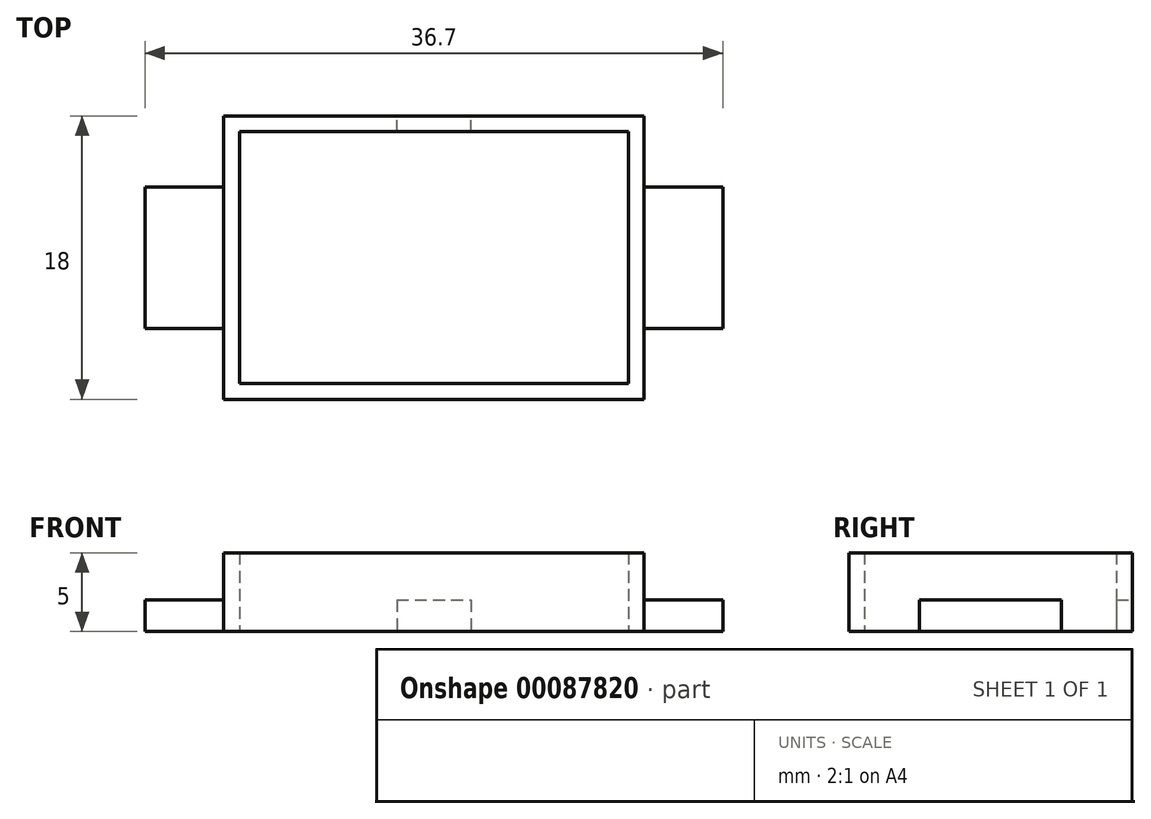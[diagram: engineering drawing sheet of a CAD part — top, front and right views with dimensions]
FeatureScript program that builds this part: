
annotation { "Feature Type Name" : "Feature", "Feature Type Description" : "" }
export const myFeature = defineFeature(function(context is Context, id is Id, definition is map)
    precondition{}
    {
        {
            var Q0;
            Q0=qCreatedBy(makeId("Top.planeOp"),FACE);
            var sketch = newSketch(context, id + "F0", { "sketchPlane" : qUnion([Q0])});
            skLineSegment(sketch, "E0.bottom", {"start": v(0, 0) * mm, "end": v(22.7, 0) * mm});
            skLineSegment(sketch, "E0.top", {"start": v(0, 14) * mm, "end": v(22.7, 14) * mm});
            skLineSegment(sketch, "E0.left", {"start": v(0, 0) * mm, "end": v(0, 4.5) * mm});
            skLineSegment(sketch, "E0.right", {"start": v(22.7, 0) * mm, "end": v(22.7, 4.5) * mm});
            skLineSegment(sketch, "E1.bottom", {"start": v(0, 4.5) * mm, "end": v(-5, 4.5) * mm});
            skLineSegment(sketch, "E1.top", {"start": v(0, 9.5) * mm, "end": v(-5, 9.5) * mm});
            skLineSegment(sketch, "E1.left", {"start": v(0, 4.5) * mm, "end": v(0, 9.5) * mm});
            skLineSegment(sketch, "E1.right", {"start": v(-5, 4.5) * mm, "end": v(-5, 9.5) * mm});
            skLineSegment(sketch, "E2.bottom", {"start": v(22.7, 4.5) * mm, "end": v(27.7, 4.5) * mm});
            skLineSegment(sketch, "E2.top", {"start": v(22.7, 9.5) * mm, "end": v(27.7, 9.5) * mm});
            skLineSegment(sketch, "E2.left", {"start": v(22.7, 4.5) * mm, "end": v(22.7, 9.5) * mm});
            skLineSegment(sketch, "E2.right", {"start": v(27.7, 4.5) * mm, "end": v(27.7, 9.5) * mm});
            skLineSegment(sketch, "E3", {"start": v(22.7, 9.5) * mm, "end": v(22.7, 14) * mm});
            skLineSegment(sketch, "E4", {"start": v(0, 9.5) * mm, "end": v(0, 14) * mm});
            skLineSegment(sketch, "E5.0", {"start": v(-2, 11.5) * mm, "end": v(-2, 16) * mm});
            skLineSegment(sketch, "E5.1", {"start": v(24.7, 2.5) * mm, "end": v(29.7, 2.5) * mm});
            skLineSegment(sketch, "E5.2", {"start": v(29.7, 2.5) * mm, "end": v(29.7, 11.5) * mm});
            skLineSegment(sketch, "E5.3", {"start": v(24.7, 11.5) * mm, "end": v(29.7, 11.5) * mm});
            skLineSegment(sketch, "E5.4", {"start": v(24.7, 11.5) * mm, "end": v(24.7, 16) * mm});
            skLineSegment(sketch, "E5.5", {"start": v(24.7, -2) * mm, "end": v(24.7, 2.5) * mm});
            skLineSegment(sketch, "E5.6", {"start": v(-2, 16) * mm, "end": v(24.7, 16) * mm});
            skLineSegment(sketch, "E5.7", {"start": v(-2, -2) * mm, "end": v(24.7, -2) * mm});
            skLineSegment(sketch, "E5.8", {"start": v(-2, -2) * mm, "end": v(-2, 2.5) * mm});
            skLineSegment(sketch, "E5.9", {"start": v(-2, 2.5) * mm, "end": v(-7, 2.5) * mm});
            skLineSegment(sketch, "E5.10", {"start": v(-7, 2.5) * mm, "end": v(-7, 11.5) * mm});
            skLineSegment(sketch, "E5.11", {"start": v(-2, 11.5) * mm, "end": v(-7, 11.5) * mm});
            skLineSegment(sketch, "E6.0", {"start": v(-1, 10.5) * mm, "end": v(-1, 15) * mm});
            skLineSegment(sketch, "E6.1", {"start": v(23.7, 3.5) * mm, "end": v(28.7, 3.5) * mm});
            skLineSegment(sketch, "E6.2", {"start": v(28.7, 3.5) * mm, "end": v(28.7, 10.5) * mm});
            skLineSegment(sketch, "E6.3", {"start": v(23.7, 10.5) * mm, "end": v(28.7, 10.5) * mm});
            skLineSegment(sketch, "E6.4", {"start": v(23.7, 10.5) * mm, "end": v(23.7, 15) * mm});
            skLineSegment(sketch, "E6.5", {"start": v(23.7, -1) * mm, "end": v(23.7, 3.5) * mm});
            skLineSegment(sketch, "E6.6", {"start": v(-1, 15) * mm, "end": v(23.7, 15) * mm});
            skLineSegment(sketch, "E6.7", {"start": v(-1, -1) * mm, "end": v(23.7, -1) * mm});
            skLineSegment(sketch, "E6.8", {"start": v(-1, -1) * mm, "end": v(-1, 3.5) * mm});
            skLineSegment(sketch, "E6.9", {"start": v(-1, 3.5) * mm, "end": v(-6, 3.5) * mm});
            skLineSegment(sketch, "E6.10", {"start": v(-6, 3.5) * mm, "end": v(-6, 10.5) * mm});
            skLineSegment(sketch, "E6.11", {"start": v(-1, 10.5) * mm, "end": v(-6, 10.5) * mm});
            skLineSegment(sketch, "E7", {"start": v(9, 14) * mm, "end": v(9, 16) * mm});
            skLineSegment(sketch, "E8", {"start": v(13.7, 14) * mm, "end": v(13.7, 16) * mm});
            skLineSegment(sketch, "E9", {"start": v(-1, 10.5) * mm, "end": v(-1, 3.5) * mm});
            skLineSegment(sketch, "E10", {"start": v(23.7, 10.5) * mm, "end": v(23.7, 3.5) * mm});
            skLineSegment(sketch, "E11", {"start": v(-2, 11.5) * mm, "end": v(-2, 2.5) * mm});
            skLineSegment(sketch, "E12", {"start": v(24.7, 11.5) * mm, "end": v(24.7, 2.5) * mm});
            skSolve(sketch);
        }
        {
            var Q0;
            {var subQ0=sQuery(id+"F0.wireOp",EDGE,"E2.right");Q0=makeQuery(id+"F0.imprint","IMPRINT",FACE,{"disambiguationData":[TD([[makeQuery(id+"F0.imprint","IMPRINT",EDGE,{"derivedFrom":subQ0}),1.0]])]});}
            var Q1;
            {var subQ10=sQuery(id+"F0.wireOp",EDGE,"E5.0");Q1=makeQuery(id+"F0.imprint","IMPRINT",FACE,{"disambiguationData":[TD([[makeQuery(id+"F0.imprint","IMPRINT",EDGE,{"derivedFrom":subQ10}),-1.0]])]});}
            var Q2;
            {var subQ0=sQuery(id+"F0.wireOp",EDGE,"E1.right");Q2=makeQuery(id+"F0.imprint","IMPRINT",FACE,{"disambiguationData":[TD([[makeQuery(id+"F0.imprint","IMPRINT",EDGE,{"derivedFrom":subQ0}),-1.0]])]});}
            var Q3;
            {var subQ1=sQuery(id+"F0.wireOp",EDGE,"E1.right");Q3=makeQuery(id+"F0.imprint","IMPRINT",FACE,{"disambiguationData":[TD([[makeQuery(id+"F0.imprint","IMPRINT",EDGE,{"derivedFrom":subQ1}),1.0]])]});}
            var Q4;
            {var subQ1=sQuery(id+"F0.wireOp",EDGE,"E2.right");Q4=makeQuery(id+"F0.imprint","IMPRINT",FACE,{"disambiguationData":[TD([[makeQuery(id+"F0.imprint","IMPRINT",EDGE,{"derivedFrom":subQ1}),-1.0]])]});}
            var Q5;
            {var subQ5=sQuery(id+"F0.wireOp",EDGE,"E5.9");Q5=makeQuery(id+"F0.imprint","IMPRINT",FACE,{"disambiguationData":[TD([[makeQuery(id+"F0.imprint","IMPRINT",EDGE,{"derivedFrom":subQ5}),-1.0]])]});}
            var Q6;
            {var subQ8=sQuery(id+"F0.wireOp",EDGE,"E5.5");Q6=makeQuery(id+"F0.imprint","IMPRINT",FACE,{"disambiguationData":[TD([[makeQuery(id+"F0.imprint","IMPRINT",EDGE,{"derivedFrom":subQ8}),1.0]])]});}
            var Q7;
            {var subQ0=sQuery(id+"F0.wireOp",EDGE,"E9");var subQ1=sQuery(id+"F0.wireOp",EDGE,"E1.bottom");var subQ2=makeQuery(id+"F0.imprint","INTERSECT",VERTEX,{"derivedFrom":[subQ1,subQ0]});Q7=makeQuery(id+"F0.imprint","IMPRINT",FACE,{"disambiguationData":[TD([[makeQuery(id+"F0.imprint","IMPRINT",EDGE,{"disambiguationData":[TD([[subQ2,-1.0]])],"derivedFrom":subQ1}),-1.0]])]});}
            var Q8;
            {var subQ0=sQuery(id+"F0.wireOp",EDGE,"E9");var subQ1=sQuery(id+"F0.wireOp",EDGE,"E1.bottom");var subQ2=makeQuery(id+"F0.imprint","INTERSECT",VERTEX,{"derivedFrom":[subQ1,subQ0]});Q8=makeQuery(id+"F0.imprint","IMPRINT",FACE,{"disambiguationData":[TD([[makeQuery(id+"F0.imprint","IMPRINT",EDGE,{"disambiguationData":[TD([[subQ2,-1.0]])],"derivedFrom":subQ1}),1.0]])]});}
            var Q9;
            {var subQ0=sQuery(id+"F0.wireOp",EDGE,"E10");var subQ1=sQuery(id+"F0.wireOp",EDGE,"E2.bottom");var subQ2=makeQuery(id+"F0.imprint","INTERSECT",VERTEX,{"derivedFrom":[subQ1,subQ0]});Q9=makeQuery(id+"F0.imprint","IMPRINT",FACE,{"disambiguationData":[TD([[makeQuery(id+"F0.imprint","IMPRINT",EDGE,{"disambiguationData":[TD([[subQ2,-1.0]])],"derivedFrom":subQ1}),-1.0]])]});}
            var Q10;
            {var subQ0=sQuery(id+"F0.wireOp",EDGE,"E10");var subQ1=sQuery(id+"F0.wireOp",EDGE,"E2.bottom");var subQ2=makeQuery(id+"F0.imprint","INTERSECT",VERTEX,{"derivedFrom":[subQ1,subQ0]});Q10=makeQuery(id+"F0.imprint","IMPRINT",FACE,{"disambiguationData":[TD([[makeQuery(id+"F0.imprint","IMPRINT",EDGE,{"disambiguationData":[TD([[subQ2,-1.0]])],"derivedFrom":subQ1}),1.0]])]});}
            var Q11;
            {var subQ0=sQuery(id+"F0.wireOp",EDGE,"E10");var subQ1=sQuery(id+"F0.wireOp",EDGE,"E2.top");var subQ2=makeQuery(id+"F0.imprint","INTERSECT",VERTEX,{"derivedFrom":[subQ1,subQ0]});Q11=makeQuery(id+"F0.imprint","IMPRINT",FACE,{"disambiguationData":[TD([[makeQuery(id+"F0.imprint","IMPRINT",EDGE,{"disambiguationData":[TD([[subQ2,-1.0]])],"derivedFrom":subQ1}),1.0]])]});}
            var Q12;
            {var subQ1=sQuery(id+"F0.wireOp",EDGE,"E5.4");Q12=makeQuery(id+"F0.imprint","IMPRINT",FACE,{"disambiguationData":[TD([[makeQuery(id+"F0.imprint","IMPRINT",EDGE,{"derivedFrom":subQ1}),1.0]])]});}
            var Q13;
            {var subQ7=sQuery(id+"F0.wireOp",EDGE,"E5.1");Q13=makeQuery(id+"F0.imprint","IMPRINT",FACE,{"disambiguationData":[TD([[makeQuery(id+"F0.imprint","IMPRINT",EDGE,{"derivedFrom":subQ7}),1.0]])]});}
            var Q14;
            {var subQ0=sQuery(id+"F0.wireOp",EDGE,"E9");var subQ1=sQuery(id+"F0.wireOp",EDGE,"E1.top");var subQ2=makeQuery(id+"F0.imprint","INTERSECT",VERTEX,{"derivedFrom":[subQ1,subQ0]});Q14=makeQuery(id+"F0.imprint","IMPRINT",FACE,{"disambiguationData":[TD([[makeQuery(id+"F0.imprint","IMPRINT",EDGE,{"disambiguationData":[TD([[subQ2,-1.0]])],"derivedFrom":subQ1}),-1.0]])]});}
            extrude(context, id + "F1", {"entities" : qUnion([Q0, Q1, Q2, Q3, Q4, Q5, Q6, Q7, Q8, Q9, Q10, Q11, Q12, Q13, Q14]), "depth" : 2 * mm});
        }
        {
            var Q0;
            {var subQ4=sQuery(id+"F0.wireOp",EDGE,"E5.0");Q0=makeQuery(id+"F0.imprint","IMPRINT",FACE,{"disambiguationData":[TD([[makeQuery(id+"F0.imprint","IMPRINT",EDGE,{"derivedFrom":subQ4}),-1.0]])]});}
            var Q1;
            {var subQ0=sQuery(id+"F0.wireOp",EDGE,"E7");var subQ1=sQuery(id+"F0.wireOp",EDGE,"E5.6");var subQ2=makeQuery(id+"F0.imprint","INTERSECT",VERTEX,{"derivedFrom":[subQ1,subQ0]});Q1=makeQuery(id+"F0.imprint","IMPRINT",FACE,{"disambiguationData":[TD([[makeQuery(id+"F0.imprint","IMPRINT",EDGE,{"disambiguationData":[TD([[subQ2,-1.0]])],"derivedFrom":subQ1}),-1.0]])]});}
            var Q2;
            {var subQ1=sQuery(id+"F0.wireOp",EDGE,"E5.4");Q2=makeQuery(id+"F0.imprint","IMPRINT",FACE,{"disambiguationData":[TD([[makeQuery(id+"F0.imprint","IMPRINT",EDGE,{"derivedFrom":subQ1}),1.0]])]});}
            var Q3;
            {var subQ0=sQuery(id+"F0.wireOp",EDGE,"E10");var subQ1=sQuery(id+"F0.wireOp",EDGE,"E2.top");var subQ2=makeQuery(id+"F0.imprint","INTERSECT",VERTEX,{"derivedFrom":[subQ1,subQ0]});Q3=makeQuery(id+"F0.imprint","IMPRINT",FACE,{"disambiguationData":[TD([[makeQuery(id+"F0.imprint","IMPRINT",EDGE,{"disambiguationData":[TD([[subQ2,-1.0]])],"derivedFrom":subQ1}),1.0]])]});}
            var Q4;
            {var subQ0=sQuery(id+"F0.wireOp",EDGE,"E10");var subQ1=sQuery(id+"F0.wireOp",EDGE,"E2.bottom");var subQ2=makeQuery(id+"F0.imprint","INTERSECT",VERTEX,{"derivedFrom":[subQ1,subQ0]});Q4=makeQuery(id+"F0.imprint","IMPRINT",FACE,{"disambiguationData":[TD([[makeQuery(id+"F0.imprint","IMPRINT",EDGE,{"disambiguationData":[TD([[subQ2,-1.0]])],"derivedFrom":subQ1}),1.0]])]});}
            var Q5;
            {var subQ8=sQuery(id+"F0.wireOp",EDGE,"E5.5");Q5=makeQuery(id+"F0.imprint","IMPRINT",FACE,{"disambiguationData":[TD([[makeQuery(id+"F0.imprint","IMPRINT",EDGE,{"derivedFrom":subQ8}),1.0]])]});}
            var Q6;
            {var subQ0=sQuery(id+"F0.wireOp",EDGE,"E10");var subQ1=sQuery(id+"F0.wireOp",EDGE,"E2.bottom");var subQ2=makeQuery(id+"F0.imprint","INTERSECT",VERTEX,{"derivedFrom":[subQ1,subQ0]});Q6=makeQuery(id+"F0.imprint","IMPRINT",FACE,{"disambiguationData":[TD([[makeQuery(id+"F0.imprint","IMPRINT",EDGE,{"disambiguationData":[TD([[subQ2,-1.0]])],"derivedFrom":subQ1}),-1.0]])]});}
            var Q7;
            {var subQ0=sQuery(id+"F0.wireOp",EDGE,"E9");var subQ1=sQuery(id+"F0.wireOp",EDGE,"E1.bottom");var subQ2=makeQuery(id+"F0.imprint","INTERSECT",VERTEX,{"derivedFrom":[subQ1,subQ0]});Q7=makeQuery(id+"F0.imprint","IMPRINT",FACE,{"disambiguationData":[TD([[makeQuery(id+"F0.imprint","IMPRINT",EDGE,{"disambiguationData":[TD([[subQ2,-1.0]])],"derivedFrom":subQ1}),1.0]])]});}
            var Q8;
            {var subQ0=sQuery(id+"F0.wireOp",EDGE,"E9");var subQ1=sQuery(id+"F0.wireOp",EDGE,"E1.bottom");var subQ2=makeQuery(id+"F0.imprint","INTERSECT",VERTEX,{"derivedFrom":[subQ1,subQ0]});Q8=makeQuery(id+"F0.imprint","IMPRINT",FACE,{"disambiguationData":[TD([[makeQuery(id+"F0.imprint","IMPRINT",EDGE,{"disambiguationData":[TD([[subQ2,-1.0]])],"derivedFrom":subQ1}),-1.0]])]});}
            var Q9;
            {var subQ0=sQuery(id+"F0.wireOp",EDGE,"E9");var subQ1=sQuery(id+"F0.wireOp",EDGE,"E1.top");var subQ2=makeQuery(id+"F0.imprint","INTERSECT",VERTEX,{"derivedFrom":[subQ1,subQ0]});Q9=makeQuery(id+"F0.imprint","IMPRINT",FACE,{"disambiguationData":[TD([[makeQuery(id+"F0.imprint","IMPRINT",EDGE,{"disambiguationData":[TD([[subQ2,-1.0]])],"derivedFrom":subQ1}),-1.0]])]});}
            var Q10;
            Q10=makeQuery(id+"F1.opExtrude","SWEPT_BODY",BODY,{"disambiguationData":[OSD([sQuery(id+"F0.wireOp",EDGE,"E0.bottom"),sQuery(id+"F0.wireOp",EDGE,"E0.top"),sQuery(id+"F0.wireOp",EDGE,"E0.left"),sQuery(id+"F0.wireOp",EDGE,"E0.right"),sQuery(id+"F0.wireOp",EDGE,"E3"),sQuery(id+"F0.wireOp",EDGE,"E2.left"),sQuery(id+"F0.wireOp",EDGE,"E1.left"),sQuery(id+"F0.wireOp",EDGE,"E4"),sQuery(id+"F0.wireOp",EDGE,"E5.0"),sQuery(id+"F0.wireOp",EDGE,"E5.1"),sQuery(id+"F0.wireOp",EDGE,"E5.2"),sQuery(id+"F0.wireOp",EDGE,"E5.3"),sQuery(id+"F0.wireOp",EDGE,"E5.4"),sQuery(id+"F0.wireOp",EDGE,"E5.5"),sQuery(id+"F0.wireOp",EDGE,"E5.6"),sQuery(id+"F0.wireOp",EDGE,"E5.7"),sQuery(id+"F0.wireOp",EDGE,"E5.8"),sQuery(id+"F0.wireOp",EDGE,"E5.9"),sQuery(id+"F0.wireOp",EDGE,"E5.10"),sQuery(id+"F0.wireOp",EDGE,"E5.11"),sQuery(id+"F0.wireOp",EDGE,"E7"),sQuery(id+"F0.wireOp",EDGE,"E8")])]});
            extrude(context, id + "F2", {"entities" : qUnion([Q0, Q1, Q2, Q3, Q4, Q5, Q6, Q7, Q8, Q9]), "operationType" : NewBodyOperationType.ADD, "endBoundEntityBody" : qUnion([Q10]), "depth" : 5 * mm});
        }
        {
            var Q0;
            {var subQ0=sQuery(id+"F0.wireOp",EDGE,"E7");var subQ1=sQuery(id+"F0.wireOp",EDGE,"E5.6");var subQ2=makeQuery(id+"F0.imprint","INTERSECT",VERTEX,{"derivedFrom":[subQ1,subQ0]});Q0=makeQuery(id+"F0.imprint","IMPRINT",FACE,{"disambiguationData":[TD([[makeQuery(id+"F0.imprint","IMPRINT",EDGE,{"disambiguationData":[TD([[subQ2,-1.0]])],"derivedFrom":subQ1}),-1.0]])]});}
            extrude(context, id + "F3", {"entities" : qUnion([Q0]), "operationType" : NewBodyOperationType.REMOVE, "depth" : 2 * mm});
        }
    });
